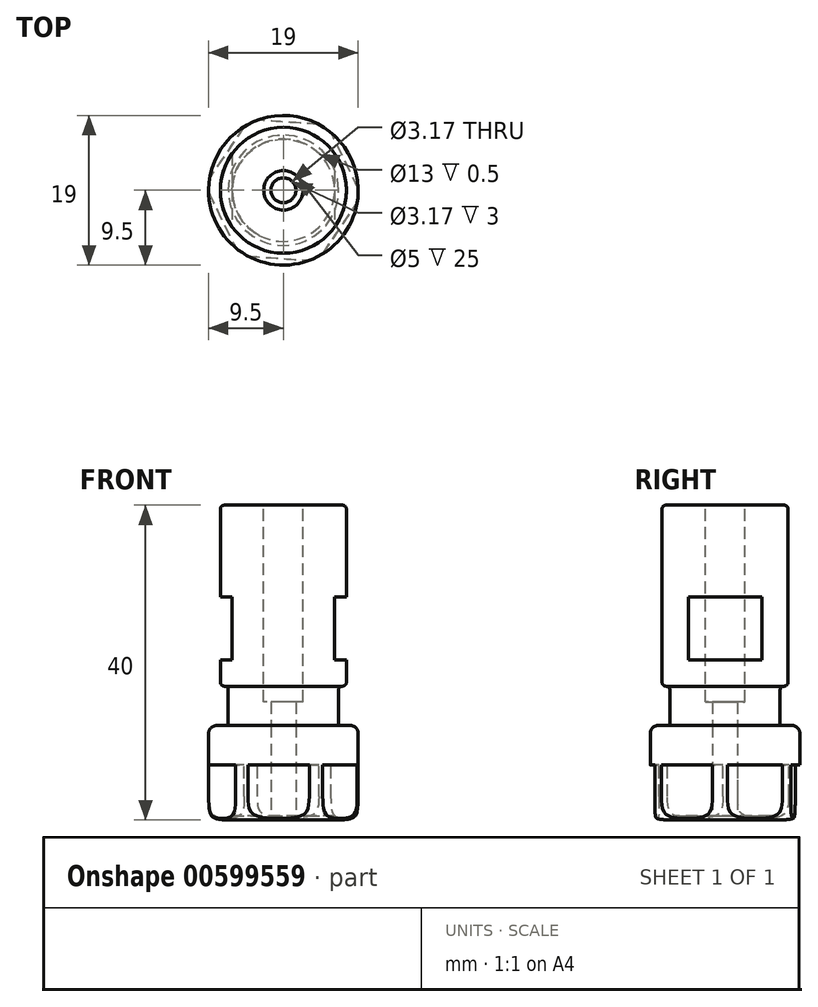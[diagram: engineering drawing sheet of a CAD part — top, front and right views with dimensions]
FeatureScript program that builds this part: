
annotation { "Feature Type Name" : "Feature", "Feature Type Description" : "" }
export const myFeature = defineFeature(function(context is Context, id is Id, definition is map)
    precondition{}
    {
        {
            var Q0;
            Q0=qCreatedBy(makeId("Top.planeOp"),FACE);
            var sketch = newSketch(context, id + "F0", { "sketchPlane" : qUnion([Q0])});
            skCircle(sketch, "E0", {"center": v(0, 0) * mm, "radius": 8 * mm});
            skSolve(sketch);
        }
        {
            var Q0;
            Q0 = qSketchRegion(id + "F0", true);
            extrude(context, id + "F1", {"entities" : qUnion([Q0]), "depth" : 28 * mm, "offsetDistance" : 25 * mm});
        }
        {
            var Q0;
            Q0=qCreatedBy(makeId("Top.planeOp"),FACE);
            var sketch = newSketch(context, id + "F2", { "sketchPlane" : qUnion([Q0])});
            skCircle(sketch, "E1", {"center": v(0, 0) * mm, "radius": 7 * mm});
            skCircle(sketch, "E2", {"center": v(0, 0) * mm, "radius": 9.32 * mm});
            skSolve(sketch);
        }
        {
            var Q0;
            Q0 = qSketchRegion(id + "F2", true);
            extrude(context, id + "F3", {"entities" : qUnion([Q0]), "operationType" : NewBodyOperationType.REMOVE, "depth" : 5 * mm, "offsetDistance" : 25 * mm});
        }
        {
            var Q0;
            Q0=makeQuery(id+"F1.opExtrude","CAP_FACE",FACE,{"disambiguationData":[OSD([sQuery(id+"F0.wireOp",EDGE,"E0")])],"isStart":true});
            var sketch = newSketch(context, id + "F4", { "sketchPlane" : qUnion([Q0])});
            skCircle(sketch, "E3", {"center": v(0, 0) * mm, "radius": 9.5 * mm});
            skSolve(sketch);
        }
        {
            var Q0;
            Q0 = qSketchRegion(id + "F4", true);
            extrude(context, id + "F5", {"entities" : qUnion([Q0]), "depth" : 12 * mm, "offsetDistance" : 25 * mm});
        }
        {
            var Q0;
            Q0=makeQuery(id+"F5.opExtrude","CAP_FACE",FACE,{"disambiguationData":[OSD([sQuery(id+"F4.wireOp",EDGE,"E3")])],"isStart":false});
            var sketch = newSketch(context, id + "F6", { "sketchPlane" : qUnion([Q0])});
            skCircle(sketch, "E4", {"center": v(0, 0) * mm, "radius": 1.59 * mm});
            skSolve(sketch);
        }
        {
            var Q0;
            Q0 = qSketchRegion(id + "F6", true);
            extrude(context, id + "F7", {"entities" : qUnion([Q0]), "operationType" : NewBodyOperationType.REMOVE, "oppositeDirection" : true, "depth" : 25 * mm, "offsetDistance" : 25 * mm});
        }
        {
            var Q0;
            Q0=makeQuery(id+"F5.opExtrude","CAP_FACE",FACE,{"disambiguationData":[OSD([sQuery(id+"F4.wireOp",EDGE,"E3")])],"isStart":false});
            var sketch = newSketch(context, id + "F8", { "sketchPlane" : qUnion([Q0])});
            skCircle(sketch, "E5.cCircle", {"center": v(0, 0) * mm, "radius": 10 * mm, "construction": true});
            skLineSegment(sketch, "E5.0", {"start": v(-5.6, 8.29) * mm, "end": v(4.38, 8.99) * mm});
            skLineSegment(sketch, "E5.1", {"start": v(4.38, 8.99) * mm, "end": v(9.98, 0.7) * mm});
            skLineSegment(sketch, "E5.2", {"start": v(9.98, 0.7) * mm, "end": v(5.6, -8.29) * mm});
            skLineSegment(sketch, "E5.3", {"start": v(5.6, -8.29) * mm, "end": v(-4.38, -8.99) * mm});
            skLineSegment(sketch, "E5.4", {"start": v(-4.38, -8.99) * mm, "end": v(-9.98, -0.7) * mm});
            skLineSegment(sketch, "E5.5", {"start": v(-9.98, -0.7) * mm, "end": v(-5.6, 8.29) * mm});
            skCircle(sketch, "E6", {"center": v(0, 0) * mm, "radius": 15.04 * mm});
            skSolve(sketch);
        }
        {
            var Q0;
            Q0 = qSketchRegion(id + "F8", true);
            extrude(context, id + "F9", {"entities" : qUnion([Q0]), "operationType" : NewBodyOperationType.REMOVE, "oppositeDirection" : true, "depth" : 7 * mm, "offsetDistance" : 25 * mm});
        }
        {
            var Q0;
            Q0=makeQuery(id+"F5.opExtrude","CAP_EDGE",EDGE,{"disambiguationData":[OSD([sQuery(id+"F4.wireOp",EDGE,"E3")])],"isStart":true});
            fillet(context, id + "F10", {"entities" : qUnion([Q0]), "radius" : 1 * mm, "tangentPropagation" : true, "allowEdgeOverflow" : false});
        }
        {
            var Q0;
            {var subQ0=sQuery(id+"F4.wireOp",EDGE,"E3");Q0=makeQuery(id+"F9.boolean.opBoolean","SPLIT",EDGE,{"disambiguationData":[TD([makeQuery(id+"F5.opExtrude","SWEPT_FACE",FACE,{"disambiguationData":[OSD([subQ0])]}),makeQuery(id+"F5.opExtrude","CAP_FACE",FACE,{"disambiguationData":[OSD([subQ0])],"isStart":false}),makeQuery(id+"F9.opExtrude","SWEPT_FACE",FACE,{"disambiguationData":[OSD([sQuery(id+"F8.wireOp",EDGE,"E5.2")])]}),makeQuery(id+"F9.opExtrude","SWEPT_FACE",FACE,{"disambiguationData":[OSD([sQuery(id+"F8.wireOp",EDGE,"E5.3")])]})])],"derivedFrom":makeQuery(id+"F5.opExtrude","CAP_EDGE",EDGE,{"disambiguationData":[OSD([subQ0])],"isStart":false})});}
            fillet(context, id + "F11", {"entities" : qUnion([Q0]), "radius" : 3 * mm, "rho" : 0.7, "crossSection" : FilletCrossSection.CONIC, "allowEdgeOverflow" : false});
        }
        {
            var Q0;
            Q0=makeQuery(id+"F1.opExtrude","CAP_FACE",FACE,{"disambiguationData":[OSD([sQuery(id+"F0.wireOp",EDGE,"E0")])],"isStart":false});
            var sketch = newSketch(context, id + "F12", { "sketchPlane" : qUnion([Q0])});
            skCircle(sketch, "E7", {"center": v(0, 0) * mm, "radius": 2.5 * mm});
            skSolve(sketch);
        }
        {
            var Q0;
            Q0 = qSketchRegion(id + "F12", true);
            extrude(context, id + "F13", {"entities" : qUnion([Q0]), "operationType" : NewBodyOperationType.REMOVE, "oppositeDirection" : true, "depth" : 25 * mm, "offsetDistance" : 25 * mm});
        }
        {
            var Q0;
            Q0=makeQuery(id+"F3.boolean.opBoolean","COPY",EDGE,{"derivedFrom":makeQuery(id+"F3.opExtrude","CAP_EDGE",EDGE,{"disambiguationData":[OSD([sQuery(id+"F2.wireOp",EDGE,"E1")])],"isStart":false})});
            var Q1;
            Q1=makeQuery(id+"F3.boolean.opBoolean","INTERSECT",EDGE,{"derivedFrom":[makeQuery(id+"F1.opExtrude","SWEPT_FACE",FACE,{"disambiguationData":[OSD([sQuery(id+"F0.wireOp",EDGE,"E0")])]}),makeQuery(id+"F3.opExtrude","CAP_FACE",FACE,{"disambiguationData":[OSD([sQuery(id+"F2.wireOp",EDGE,"E1"),sQuery(id+"F2.wireOp",EDGE,"E2")])],"isStart":false})]});
            var Q2;
            Q2=makeQuery(id+"F1.opExtrude","CAP_EDGE",EDGE,{"disambiguationData":[OSD([sQuery(id+"F0.wireOp",EDGE,"E0")])],"isStart":false});
            fillet(context, id + "F14", {"entities" : qUnion([Q0, Q1, Q2]), "radius" : 0.5 * mm, "tangentPropagation" : true, "allowEdgeOverflow" : false});
        }
        {
            var Q0;
            Q0=qCreatedBy(makeId("Front.planeOp"),FACE);
            var sketch = newSketch(context, id + "F15", { "sketchPlane" : qUnion([Q0])});
            skLineSegment(sketch, "E8.bottom", {"start": v(12.44, 8.34) * mm, "end": v(6.5, 8.34) * mm});
            skLineSegment(sketch, "E8.top", {"start": v(12.44, 16.34) * mm, "end": v(6.5, 16.34) * mm});
            skLineSegment(sketch, "E8.left", {"start": v(12.44, 8.34) * mm, "end": v(12.44, 16.34) * mm});
            skLineSegment(sketch, "E8.right", {"start": v(6.5, 8.34) * mm, "end": v(6.5, 16.34) * mm});
            skLineSegment(sketch, "E9", {"start": v(0, 0) * mm, "end": v(0, 36.17) * mm, "construction": true});
            skLineSegment(sketch, "E10.MirrorCS", {"start": v(-12.44, 8.34) * mm, "end": v(-6.5, 8.34) * mm});
            skLineSegment(sketch, "E11.MirrorCS", {"start": v(-12.44, 16.34) * mm, "end": v(-6.5, 16.34) * mm});
            skLineSegment(sketch, "E12.MirrorCS", {"start": v(-6.5, 8.34) * mm, "end": v(-6.5, 16.34) * mm});
            skLineSegment(sketch, "E13.MirrorCS", {"start": v(-12.44, 8.34) * mm, "end": v(-12.44, 16.34) * mm});
            skSolve(sketch);
        }
        {
            var Q0;
            Q0 = qSketchRegion(id + "F15", true);
            extrude(context, id + "F16", {"entities" : qUnion([Q0]), "operationType" : NewBodyOperationType.REMOVE, "oppositeDirection" : true, "depth" : 25 * mm, "offsetDistance" : 25 * mm, "symmetric" : true});
        }
        {
            var Q0;
            Q0=makeQuery(id+"F5.opExtrude","CAP_FACE",FACE,{"disambiguationData":[OSD([sQuery(id+"F4.wireOp",EDGE,"E3")])],"isStart":false});
            extrude(context, id + "F17", {"entities" : qUnion([Q0]), "operationType" : NewBodyOperationType.REMOVE, "oppositeDirection" : true, "depth" : 0.5 * mm, "offsetDistance" : 25 * mm});
        }
    });
